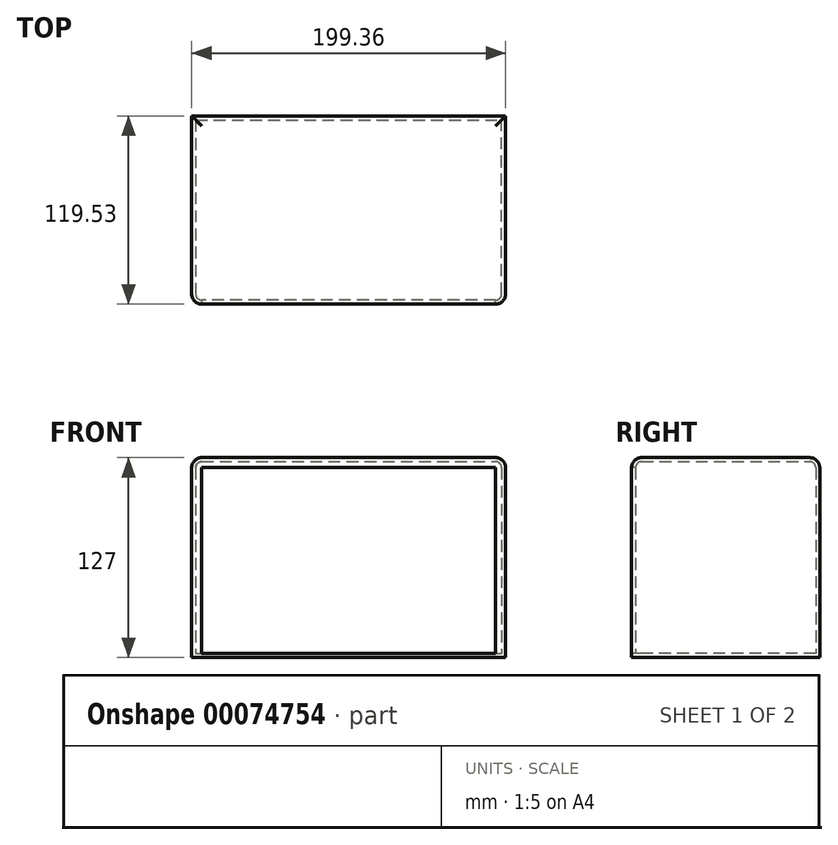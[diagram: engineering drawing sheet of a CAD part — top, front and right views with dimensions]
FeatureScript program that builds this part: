
annotation { "Feature Type Name" : "Feature", "Feature Type Description" : "" }
export const myFeature = defineFeature(function(context is Context, id is Id, definition is map)
    precondition{}
    {
        {
            var Q0;
            Q0=qCreatedBy(makeId("Top.planeOp"),FACE);
            var sketch = newSketch(context, id + "F0", { "sketchPlane" : qUnion([Q0])});
            skLineSegment(sketch, "E0.bottom", {"start": v(-120.63, 61.25) * mm, "end": v(78.73, 61.25) * mm});
            skLineSegment(sketch, "E0.top", {"start": v(-120.63, -58.28) * mm, "end": v(78.73, -58.28) * mm});
            skLineSegment(sketch, "E0.left", {"start": v(-120.63, 61.25) * mm, "end": v(-120.63, -58.28) * mm});
            skLineSegment(sketch, "E0.right", {"start": v(78.73, 61.25) * mm, "end": v(78.73, -58.28) * mm});
            skSolve(sketch);
        }
        {
            var Q0;
            Q0=makeQuery(id+"F0.imprint","IMPRINT",FACE,{"disambiguationData":[TD([[makeQuery(id+"F0.imprint","IMPRINT",EDGE,{"derivedFrom":sQuery(id+"F0.wireOp",EDGE,"E0.bottom")}),-1.0]])]});
            extrude(context, id + "F1", {"entities" : qUnion([Q0]), "depth" : 127 * mm});
        }
        {
            var Q0;
            Q0=makeQuery(id+"F1.opExtrude","CAP_EDGE",EDGE,{"disambiguationData":[OSD([sQuery(id+"F0.wireOp",EDGE,"E0.top")])],"isStart":false});
            var Q1;
            Q1=makeQuery(id+"F1.opExtrude","CAP_EDGE",EDGE,{"disambiguationData":[OSD([sQuery(id+"F0.wireOp",EDGE,"E0.right")])],"isStart":false});
            var Q2;
            Q2=makeQuery(id+"F1.opExtrude","CAP_EDGE",EDGE,{"disambiguationData":[OSD([sQuery(id+"F0.wireOp",EDGE,"E0.bottom")])],"isStart":false});
            var Q3;
            Q3=makeQuery(id+"F1.opExtrude","CAP_EDGE",EDGE,{"disambiguationData":[OSD([sQuery(id+"F0.wireOp",EDGE,"E0.left")])],"isStart":false});
            var Q4;
            Q4=makeQuery(id+"F1.opExtrude","SWEPT_EDGE",EDGE,{"disambiguationData":[OSD([sQuery(id+"F0.wireOp",EDGE,"E0.top"),sQuery(id+"F0.wireOp",EDGE,"E0.left")])]});
            var Q5;
            Q5=makeQuery(id+"F1.opExtrude","SWEPT_EDGE",EDGE,{"disambiguationData":[OSD([sQuery(id+"F0.wireOp",EDGE,"E0.top"),sQuery(id+"F0.wireOp",EDGE,"E0.right")])]});
            fillet(context, id + "F2", {"entities" : qUnion([Q0, Q1, Q2, Q3, Q4, Q5]), "radius" : 6.35 * mm, "tangentPropagation" : true, "allowEdgeOverflow" : false});
        }
        {
            var Q0;
            Q0=makeQuery(id+"F1.opExtrude","SWEPT_FACE",FACE,{"disambiguationData":[OSD([sQuery(id+"F0.wireOp",EDGE,"E0.top")])]});
            shell(context, id + "F3", {"entities" : qUnion([Q0]), "thickness" : 2.54 * mm});
        }
    });
